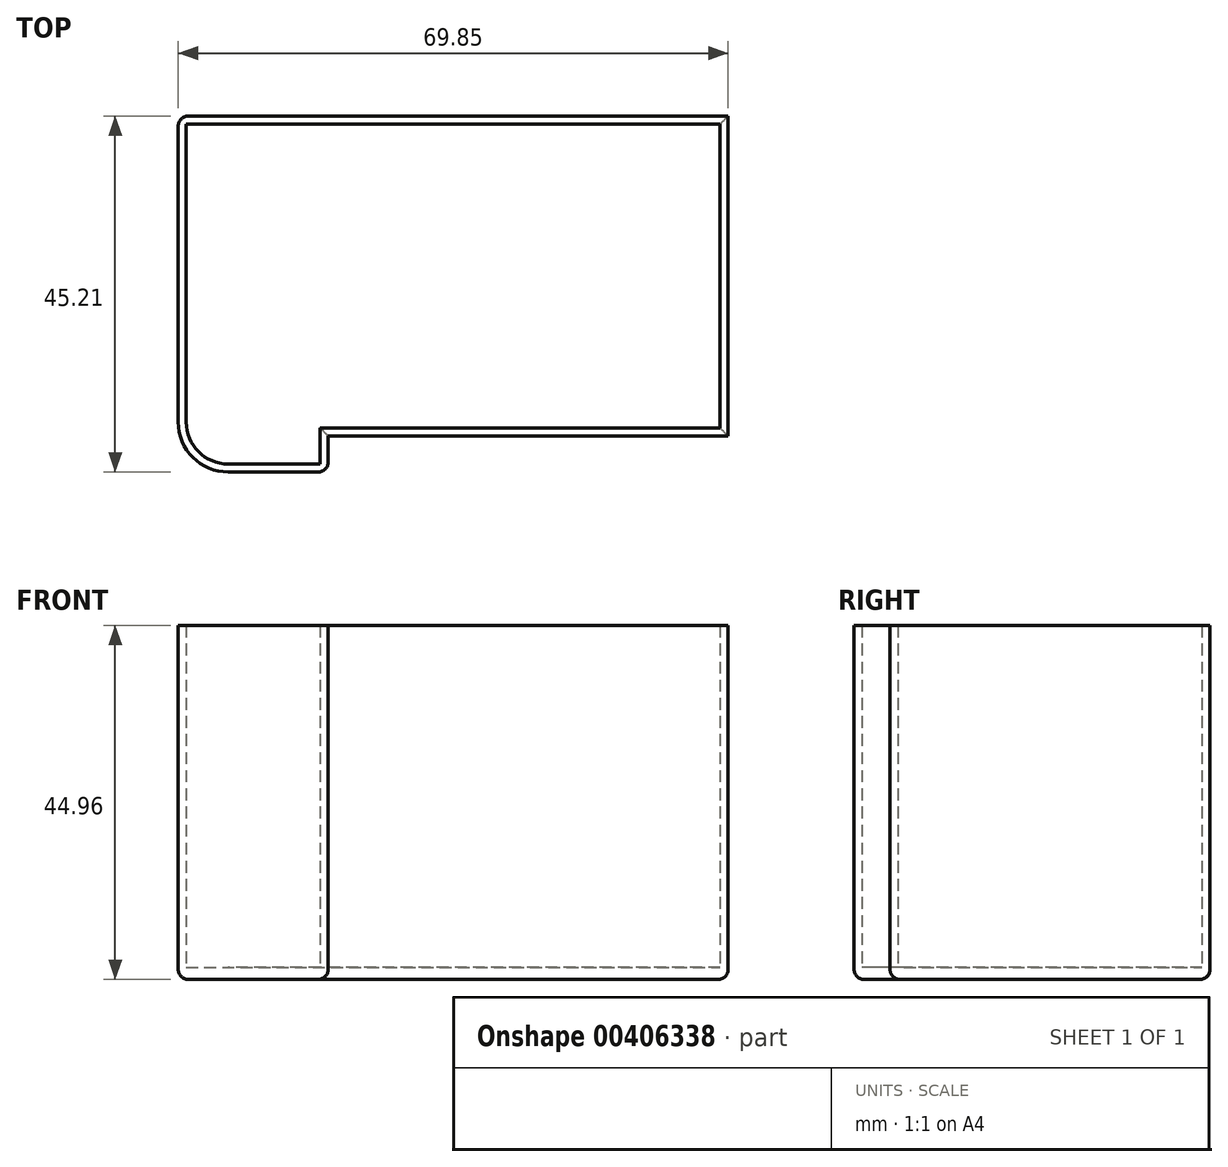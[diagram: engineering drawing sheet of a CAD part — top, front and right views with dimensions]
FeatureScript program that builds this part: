
annotation { "Feature Type Name" : "Feature", "Feature Type Description" : "" }
export const myFeature = defineFeature(function(context is Context, id is Id, definition is map)
    precondition{}
    {
        {
            var Q0;
            Q0=qCreatedBy(makeId("Top.planeOp"),FACE);
            var sketch = newSketch(context, id + "F0", { "sketchPlane" : qUnion([Q0])});
            skLineSegment(sketch, "E0", {"start": v(-35.58, -17.32) * mm, "end": v(-35.58, 21.54) * mm});
            skLineSegment(sketch, "E1", {"start": v(-35.58, 21.54) * mm, "end": v(34.27, 21.54) * mm});
            skLineSegment(sketch, "E2", {"start": v(34.27, 21.54) * mm, "end": v(34.27, -19.1) * mm});
            skLineSegment(sketch, "E3", {"start": v(34.27, -19.1) * mm, "end": v(-16.53, -19.1) * mm});
            skLineSegment(sketch, "E4", {"start": v(-16.53, -19.1) * mm, "end": v(-16.53, -23.67) * mm});
            skLineSegment(sketch, "E5", {"start": v(-16.53, -23.67) * mm, "end": v(-29.23, -23.67) * mm});
            skPoint(sketch, "E6.visualSharp", {"position": v(-35.58, -23.67) * mm});
            skArc(sketch, "E6.filletArc", {"start": v(-35.58, -17.32) * mm, "mid": v(-33.72, -21.81) * mm, "end": v(-29.23, -23.67) * mm});
            skSolve(sketch);
        }
        {
            var Q0;
            Q0=makeQuery(id+"F0.imprint","IMPRINT",FACE,{"disambiguationData":[TD([[makeQuery(id+"F0.imprint","IMPRINT",EDGE,{"derivedFrom":sQuery(id+"F0.wireOp",EDGE,"E0")}),-1.0]])]});
            extrude(context, id + "F1", {"entities" : qUnion([Q0]), "depth" : 1.52 * mm});
        }
        {
            var Q0;
            Q0=makeQuery(id+"F1.opExtrude","CAP_FACE",FACE,{"disambiguationData":[OSD([sQuery(id+"F0.wireOp",EDGE,"E0"),sQuery(id+"F0.wireOp",EDGE,"E1"),sQuery(id+"F0.wireOp",EDGE,"E2"),sQuery(id+"F0.wireOp",EDGE,"E3"),sQuery(id+"F0.wireOp",EDGE,"E4"),sQuery(id+"F0.wireOp",EDGE,"E5"),sQuery(id+"F0.wireOp",EDGE,"E6.filletArc")])],"isStart":false});
            var sketch = newSketch(context, id + "F2", { "sketchPlane" : qUnion([Q0])});
            skLineSegment(sketch, "E7", {"start": v(-35.58, -17.32) * mm, "end": v(-35.58, 21.54) * mm});
            skLineSegment(sketch, "E8", {"start": v(-35.58, 21.54) * mm, "end": v(34.27, 21.54) * mm});
            skLineSegment(sketch, "E9", {"start": v(34.27, 21.54) * mm, "end": v(34.27, -19.1) * mm});
            skLineSegment(sketch, "E10", {"start": v(34.27, -19.1) * mm, "end": v(-16.53, -19.1) * mm});
            skLineSegment(sketch, "E11", {"start": v(-16.53, -19.1) * mm, "end": v(-16.53, -23.67) * mm});
            skLineSegment(sketch, "E12", {"start": v(-16.53, -23.67) * mm, "end": v(-29.23, -23.67) * mm});
            skPoint(sketch, "E13.visualSharp", {"position": v(-35.58, -23.67) * mm});
            skArc(sketch, "E13.filletArc", {"start": v(-35.58, -17.32) * mm, "mid": v(-33.72, -21.81) * mm, "end": v(-29.23, -23.67) * mm});
            skLineSegment(sketch, "E14.0", {"start": v(-17.55, -18.09) * mm, "end": v(-17.55, -22.66) * mm});
            skLineSegment(sketch, "E14.1", {"start": v(-34.56, -17.32) * mm, "end": v(-34.56, 20.52) * mm});
            skLineSegment(sketch, "E14.2", {"start": v(-34.56, 20.52) * mm, "end": v(33.25, 20.52) * mm});
            skLineSegment(sketch, "E14.3", {"start": v(-17.55, -22.66) * mm, "end": v(-29.23, -22.66) * mm});
            skLineSegment(sketch, "E14.4", {"start": v(33.25, 20.52) * mm, "end": v(33.25, -18.09) * mm});
            skLineSegment(sketch, "E14.5", {"start": v(33.25, -18.09) * mm, "end": v(-17.55, -18.09) * mm});
            skPoint(sketch, "E15.visualSharp", {"position": v(-34.56, -22.66) * mm});
            skArc(sketch, "E15.filletArc", {"start": v(-34.56, -17.32) * mm, "mid": v(-33, -21.1) * mm, "end": v(-29.23, -22.66) * mm});
            skSolve(sketch);
        }
        {
            var Q0;
            Q0 = qSketchRegion(id + "F2", true);
            extrude(context, id + "F3", {"entities" : qUnion([Q0]), "operationType" : NewBodyOperationType.ADD, "depth" : 43.43 * mm});
        }
        {
            var Q0;
            Q0=makeQuery(id+"F1.opExtrude","CAP_FACE",FACE,{"disambiguationData":[OSD([sQuery(id+"F0.wireOp",EDGE,"E0"),sQuery(id+"F0.wireOp",EDGE,"E1"),sQuery(id+"F0.wireOp",EDGE,"E2"),sQuery(id+"F0.wireOp",EDGE,"E3"),sQuery(id+"F0.wireOp",EDGE,"E4"),sQuery(id+"F0.wireOp",EDGE,"E5"),sQuery(id+"F0.wireOp",EDGE,"E6.filletArc")])],"isStart":true});
            fillet(context, id + "F4", {"entities" : qUnion([Q0]), "radius" : 1.27 * mm, "tangentPropagation" : true, "allowEdgeOverflow" : false});
        }
        {
            var Q0;
            Q0=makeQuery(id+"F3.boolean.opBoolean","MERGE",EDGE,{"derivedFrom":[makeQuery(id+"F1.opExtrude","SWEPT_EDGE",EDGE,{"disambiguationData":[OSD([sQuery(id+"F0.wireOp",EDGE,"E4"),sQuery(id+"F0.wireOp",EDGE,"E5")])]}),makeQuery(id+"F3.opExtrude","SWEPT_EDGE",EDGE,{"disambiguationData":[OSD([sQuery(id+"F2.wireOp",EDGE,"E11"),sQuery(id+"F2.wireOp",EDGE,"E12")])]})]});
            var Q1;
            Q1=makeQuery(id+"F3.boolean.opBoolean","MERGE",EDGE,{"derivedFrom":[makeQuery(id+"F1.opExtrude","SWEPT_EDGE",EDGE,{"disambiguationData":[OSD([sQuery(id+"F0.wireOp",EDGE,"E0"),sQuery(id+"F0.wireOp",EDGE,"E1")])]}),makeQuery(id+"F3.opExtrude","SWEPT_EDGE",EDGE,{"disambiguationData":[OSD([sQuery(id+"F2.wireOp",EDGE,"E7"),sQuery(id+"F2.wireOp",EDGE,"E8")])]})]});
            fillet(context, id + "F5", {"entities" : qUnion([Q0, Q1]), "radius" : 1.27 * mm, "tangentPropagation" : true, "allowEdgeOverflow" : false});
        }
    });
